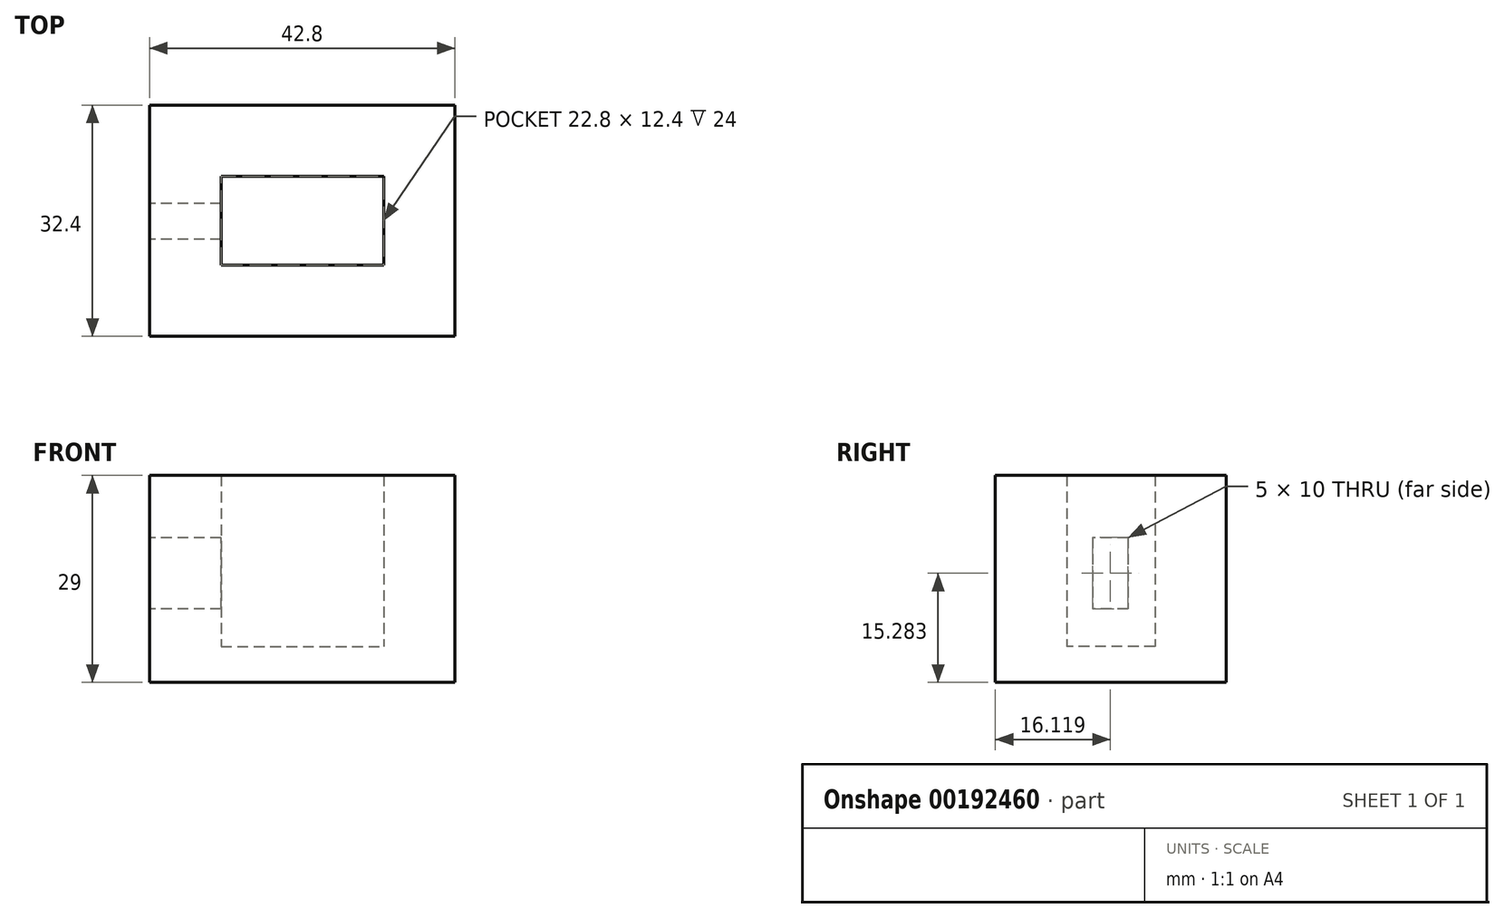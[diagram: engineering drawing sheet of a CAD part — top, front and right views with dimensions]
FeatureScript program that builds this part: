
annotation { "Feature Type Name" : "Feature", "Feature Type Description" : "" }
export const myFeature = defineFeature(function(context is Context, id is Id, definition is map)
    precondition{}
    {
        {
            var Q0;
            Q0=qCreatedBy(makeId("Top.planeOp"),FACE);
            var sketch = newSketch(context, id + "F0", { "sketchPlane" : qUnion([Q0])});
            skLineSegment(sketch, "E0.bottom", {"start": v(-11.4, 6.2) * mm, "end": v(11.4, 6.2) * mm});
            skLineSegment(sketch, "E0.top", {"start": v(-11.4, -6.2) * mm, "end": v(11.4, -6.2) * mm});
            skLineSegment(sketch, "E0.left", {"start": v(-11.4, 6.2) * mm, "end": v(-11.4, -6.2) * mm});
            skLineSegment(sketch, "E0.right", {"start": v(11.4, 6.2) * mm, "end": v(11.4, -6.2) * mm});
            skLineSegment(sketch, "E1.bottom", {"start": v(-21.4, -16.2) * mm, "end": v(21.4, -16.2) * mm});
            skLineSegment(sketch, "E1.top", {"start": v(-21.4, 16.2) * mm, "end": v(21.4, 16.2) * mm});
            skLineSegment(sketch, "E1.left", {"start": v(-21.4, -16.2) * mm, "end": v(-21.4, 16.2) * mm});
            skLineSegment(sketch, "E1.right", {"start": v(21.4, -16.2) * mm, "end": v(21.4, 16.2) * mm});
            skPoint(sketch, "E2", {"position": v(21.4, 0) * mm});
            skPoint(sketch, "E3", {"position": v(0, 16.2) * mm});
            skSolve(sketch);
        }
        {
            var Q0;
            Q0=makeQuery(id+"F0.imprint","IMPRINT",FACE,{"disambiguationData":[TD([[makeQuery(id+"F0.imprint","IMPRINT",EDGE,{"derivedFrom":sQuery(id+"F0.wireOp",EDGE,"E0.bottom")}),1.0]])]});
            extrude(context, id + "F1", {"entities" : qUnion([Q0]), "depth" : 24 * mm});
        }
        {
            var Q0;
            Q0=makeQuery(id+"F1.opExtrude","CAP_FACE",FACE,{"disambiguationData":[OSD([sQuery(id+"F0.wireOp",EDGE,"E0.bottom"),sQuery(id+"F0.wireOp",EDGE,"E0.top"),sQuery(id+"F0.wireOp",EDGE,"E0.left"),sQuery(id+"F0.wireOp",EDGE,"E0.right"),sQuery(id+"F0.wireOp",EDGE,"E1.bottom"),sQuery(id+"F0.wireOp",EDGE,"E1.top"),sQuery(id+"F0.wireOp",EDGE,"E1.left"),sQuery(id+"F0.wireOp",EDGE,"E1.right")])],"isStart":true});
            var sketch = newSketch(context, id + "F2", { "sketchPlane" : qUnion([Q0])});
            skLineSegment(sketch, "E4.0.0", {"start": v(-21.4, 16.2) * mm, "end": v(-21.4, -16.2) * mm});
            skLineSegment(sketch, "E4.0.1", {"start": v(-21.4, -16.2) * mm, "end": v(21.4, -16.2) * mm});
            skLineSegment(sketch, "E4.0.2", {"start": v(21.4, -16.2) * mm, "end": v(21.4, 16.2) * mm});
            skLineSegment(sketch, "E4.0.3", {"start": v(21.4, 16.2) * mm, "end": v(-21.4, 16.2) * mm});
            skLineSegment(sketch, "E5.bottom", {"start": v(-21.4, 16.2) * mm, "end": v(21.4, 16.2) * mm});
            skLineSegment(sketch, "E5.right", {"start": v(21.4, 16.2) * mm, "end": v(21.4, -16.2) * mm});
            skSolve(sketch);
        }
        {
            var Q0;
            Q0 = qSketchRegion(id + "F2", true);
            extrude(context, id + "F3", {"entities" : qUnion([Q0]), "operationType" : NewBodyOperationType.ADD, "depth" : 5 * mm});
        }
        {
            var Q0;
            Q0=makeQuery(id+"F3.boolean.opBoolean","MERGE",FACE,{"derivedFrom":[makeQuery(id+"F1.opExtrude","SWEPT_FACE",FACE,{"disambiguationData":[OSD([sQuery(id+"F0.wireOp",EDGE,"E1.left")])]}),makeQuery(id+"F3.opExtrude","SWEPT_FACE",FACE,{"disambiguationData":[OSD([sQuery(id+"F2.wireOp",EDGE,"E4.0.0")])]})]});
            var sketch = newSketch(context, id + "F4", { "sketchPlane" : qUnion([Q0])});
            skLineSegment(sketch, "E6.bottom", {"start": v(-2.42, 15.28) * mm, "end": v(2.58, 15.28) * mm});
            skLineSegment(sketch, "E6.top", {"start": v(-2.42, 5.28) * mm, "end": v(2.58, 5.28) * mm});
            skLineSegment(sketch, "E6.left", {"start": v(-2.42, 15.28) * mm, "end": v(-2.42, 5.28) * mm});
            skLineSegment(sketch, "E6.right", {"start": v(2.58, 15.28) * mm, "end": v(2.58, 5.28) * mm});
            skSolve(sketch);
        }
        {
            var Q0;
            Q0=makeQuery(id+"F4.imprint","IMPRINT",FACE,{"disambiguationData":[TD([[makeQuery(id+"F4.imprint","IMPRINT",EDGE,{"derivedFrom":sQuery(id+"F4.wireOp",EDGE,"E6.bottom")}),-1.0]])]});
            extrude(context, id + "F5", {"entities" : qUnion([Q0]), "operationType" : NewBodyOperationType.REMOVE, "oppositeDirection" : true, "depth" : 25.4 * mm});
        }
    });
